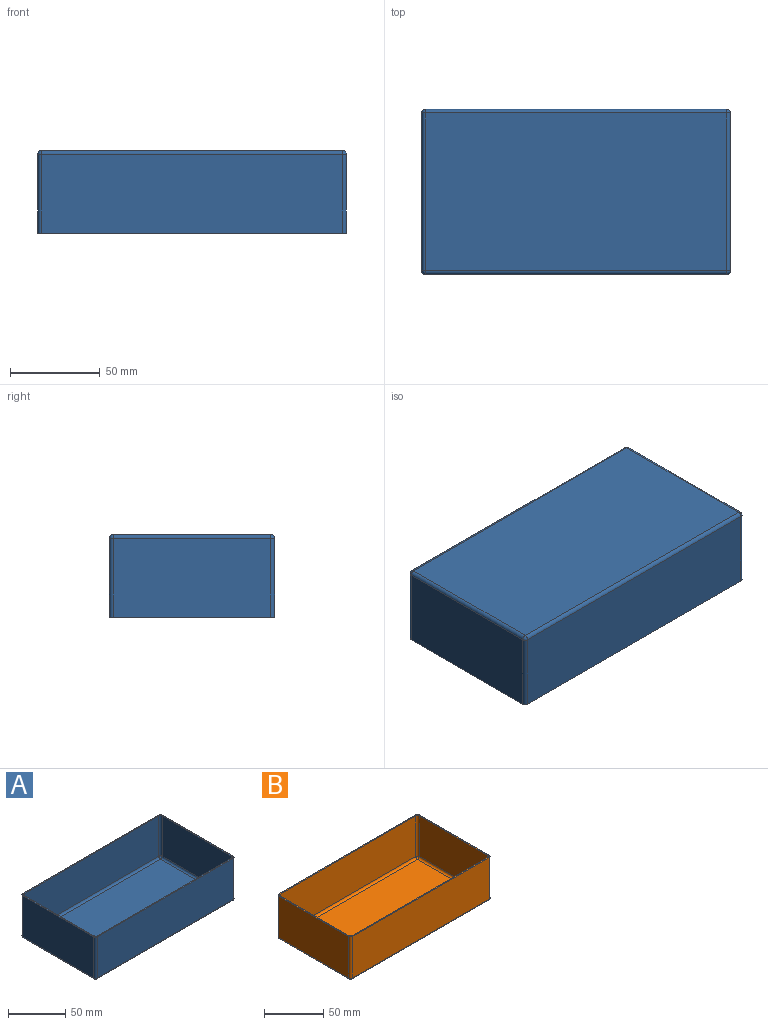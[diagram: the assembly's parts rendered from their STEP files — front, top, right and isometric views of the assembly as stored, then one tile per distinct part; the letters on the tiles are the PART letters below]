
ASSEMBLY  parts=2 mates=1
PART A: 35 faces, bbox 172x92x46 mm
  f0: plane 168x44mm, normal (0,-1,0), area 7392mm2, adj f9,f23,f26,f33
  f1: plane 88x44mm, normal (1,0,0), area 3872mm2, adj f9,f23,f24,f32
  f2: plane 168x44mm, normal (0,1,0), area 7392mm2, adj f9,f24,f25,f28
  f3: plane 88x44mm, normal (-1,0,0), area 3872mm2, adj f9,f25,f26,f29
  f4: plane 168x88mm, normal (0,0,-1), area 14784mm2, adj f28,f29,f32,f33
  f5: plane 86x43mm, normal (1,0,0), area 3698mm2, adj f9,f16,f20,f22
  f6: plane 166x43mm, normal (0,-1,0), area 7138mm2, adj f9,f13,f19,f22
  f7: plane 86x43mm, normal (-1,0,0), area 3698mm2, adj f9,f11,f13,f14
  f8: plane 166x43mm, normal (0,1,0), area 7138mm2, adj f9,f11,f15,f16
  f9: plane 172x92mm, normal (0,0,1), area 524mm2, adj f0,f1,f2,f3,f5,f6,f7,f8
  f10: plane 166x86mm, normal (0,0,1), area 14276mm2, adj f14,f15,f19,f20
  f11: cylinder r=2mm len=43mm, axis (0,0,-1), area 135.1mm2, adj f7,f8,f9,f12
  f12: sphere r=2mm, area 6.3mm2, adj f11,f14,f15
  f13: cylinder r=2mm len=43mm, axis (0,0,1), area 135.1mm2, adj f6,f7,f9,f17
  f14: cylinder r=2mm len=86mm, axis (0,-1,0), area 270.2mm2, adj f7,f10,f12,f17
  f15: cylinder r=2mm len=166mm, axis (-1,0,0), area 521.5mm2, adj f8,f10,f12,f18
  f16: cylinder r=2mm len=43mm, axis (0,0,1), area 135.1mm2, adj f5,f8,f9,f18
  f17: sphere r=2mm, area 6.3mm2, adj f13,f14,f19
  f18: sphere r=2mm, area 6.3mm2, adj f15,f16,f20
  f19: cylinder r=2mm len=166mm, axis (1,0,0), area 521.5mm2, adj f6,f10,f17,f21
  f20: cylinder r=2mm len=86mm, axis (0,1,0), area 270.2mm2, adj f5,f10,f18,f21
  f21: sphere r=2mm, area 6.3mm2, adj f19,f20,f22
  f22: cylinder r=2mm len=43mm, axis (0,0,-1), area 135.1mm2, adj f5,f6,f9,f21
  f23: cylinder r=2mm len=44mm, axis (0,0,1), area 138.2mm2, adj f0,f1,f9,f34
  f24: cylinder r=2mm len=44mm, axis (0,0,-1), area 138.2mm2, adj f1,f2,f9,f30
  f25: cylinder r=2mm len=44mm, axis (0,0,1), area 138.2mm2, adj f2,f3,f9,f27
  f26: cylinder r=2mm len=44mm, axis (0,0,-1), area 138.2mm2, adj f0,f3,f9,f31
  f27: sphere r=2mm, area 6.3mm2, adj f25,f28,f29
  f28: cylinder r=2mm len=168mm, axis (-1,0,0), area 527.8mm2, adj f2,f4,f27,f30
  f29: cylinder r=2mm len=88mm, axis (0,-1,0), area 276.5mm2, adj f3,f4,f27,f31
  f30: sphere r=2mm, area 6.3mm2, adj f24,f28,f32
  f31: sphere r=2mm, area 6.3mm2, adj f26,f29,f33
  f32: cylinder r=2mm len=88mm, axis (0,1,0), area 276.5mm2, adj f1,f4,f30,f34
  f33: cylinder r=2mm len=168mm, axis (1,0,0), area 527.8mm2, adj f0,f4,f31,f34
  f34: sphere r=2mm, area 6.3mm2, adj f23,f32,f33
PART B: 35 faces, bbox 168x88x45 mm
  f0: plane 164x43mm, normal (0,-1,0), area 7052mm2, adj f9,f23,f26,f33
  f1: plane 84x43mm, normal (1,0,0), area 3612mm2, adj f9,f23,f24,f32
  f2: plane 164x43mm, normal (0,1,0), area 7052mm2, adj f9,f24,f25,f28
  f3: plane 84x43mm, normal (-1,0,0), area 3612mm2, adj f9,f25,f26,f29
  f4: plane 164x84mm, normal (0,0,-1), area 13776mm2, adj f28,f29,f32,f33
  f5: plane 82x42mm, normal (1,0,0), area 3444mm2, adj f9,f16,f20,f22
  f6: plane 162x42mm, normal (0,-1,0), area 6804mm2, adj f9,f13,f19,f22
  f7: plane 82x42mm, normal (-1,0,0), area 3444mm2, adj f9,f11,f13,f14
  f8: plane 162x42mm, normal (0,1,0), area 6804mm2, adj f9,f11,f15,f16
  f9: plane 168x88mm, normal (0,0,1), area 508mm2, adj f0,f1,f2,f3,f5,f6,f7,f8
  f10: plane 162x82mm, normal (0,0,1), area 13284mm2, adj f14,f15,f19,f20
  f11: cylinder r=2mm len=42mm, axis (0,0,-1), area 131.9mm2, adj f7,f8,f9,f12
  f12: sphere r=2mm, area 6.3mm2, adj f11,f14,f15
  f13: cylinder r=2mm len=42mm, axis (0,0,1), area 131.9mm2, adj f6,f7,f9,f17
  f14: cylinder r=2mm len=82mm, axis (0,-1,0), area 257.6mm2, adj f7,f10,f12,f17
  f15: cylinder r=2mm len=162mm, axis (-1,0,0), area 508.9mm2, adj f8,f10,f12,f18
  f16: cylinder r=2mm len=42mm, axis (0,0,1), area 131.9mm2, adj f5,f8,f9,f18
  f17: sphere r=2mm, area 6.3mm2, adj f13,f14,f19
  f18: sphere r=2mm, area 6.3mm2, adj f15,f16,f20
  f19: cylinder r=2mm len=162mm, axis (1,0,0), area 508.9mm2, adj f6,f10,f17,f21
  f20: cylinder r=2mm len=82mm, axis (0,1,0), area 257.6mm2, adj f5,f10,f18,f21
  f21: sphere r=2mm, area 6.3mm2, adj f19,f20,f22
  f22: cylinder r=2mm len=42mm, axis (0,0,-1), area 131.9mm2, adj f5,f6,f9,f21
  f23: cylinder r=2mm len=43mm, axis (0,0,1), area 135.1mm2, adj f0,f1,f9,f34
  f24: cylinder r=2mm len=43mm, axis (0,0,-1), area 135.1mm2, adj f1,f2,f9,f30
  f25: cylinder r=2mm len=43mm, axis (0,0,1), area 135.1mm2, adj f2,f3,f9,f27
  f26: cylinder r=2mm len=43mm, axis (0,0,-1), area 135.1mm2, adj f0,f3,f9,f31
  f27: sphere r=2mm, area 6.3mm2, adj f25,f28,f29
  f28: cylinder r=2mm len=164mm, axis (-1,0,0), area 515.2mm2, adj f2,f4,f27,f30
  f29: cylinder r=2mm len=84mm, axis (0,-1,0), area 263.9mm2, adj f3,f4,f27,f31
  f30: sphere r=2mm, area 6.3mm2, adj f24,f28,f32
  f31: sphere r=2mm, area 6.3mm2, adj f26,f29,f33
  f32: cylinder r=2mm len=84mm, axis (0,1,0), area 263.9mm2, adj f1,f4,f30,f34
  f33: cylinder r=2mm len=164mm, axis (1,0,0), area 515.2mm2, adj f0,f4,f31,f34
  f34: sphere r=2mm, area 6.3mm2, adj f23,f32,f33
PLACE A rot(axis=(0,1,0),180deg) t=(-21.25,-29.8,-3.3)mm
PLACE B t=(-21.25,-29.8,-49.3)mm
MATE planar A.f10 <-> B.f9  axis (0,0,-1) through (-21.25,-29.8,-4.3)mm
